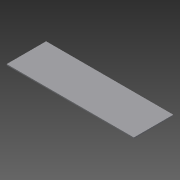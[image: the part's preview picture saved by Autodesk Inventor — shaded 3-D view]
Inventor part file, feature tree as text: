
AUTODESK INVENTOR PART (.ipt)
format: ipt  version: 2013 (Build 170138000, 138)  size: 64,000 bytes
history: native  units: in
note: dims shown in document units (in); Inventor stores cm internally (conversion verified against a paired STEP export)
features: extrude x1, sketch x1
ambient origin geometry x8: Origin, YZ Plane, XZ Plane, XY Plane, X Axis, Y Axis, Z Axis, Center Point
bodies: Solid1 (feature_tree)
feature tree (2):
  extrude  "Extrusion1"  Depth=18.0in
  sketch  "Sketch1"  dims[d0=58.0in d1=18.0in d2=0.5in d3=0.0in]
